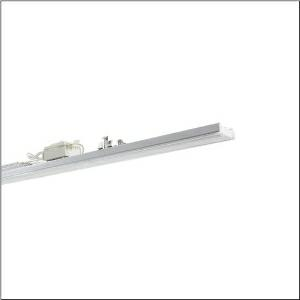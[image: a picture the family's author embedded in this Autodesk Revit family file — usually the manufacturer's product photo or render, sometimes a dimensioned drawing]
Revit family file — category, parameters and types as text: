
# Revit family: licross_r__21_recessed_ho_52te12mn4fxm_584e
name_source: partatom
category: Lighting Fixtures
units: mm (PartAtom-declared; Revit-internal decimal feet)

## family parameters
Cut with Voids When Loaded = No
Host = Face
Light Source = No
Part Type = Normal
Room Calculation Point = No
Round Connector Dimension = Use Diameter
Shared = No

## types (1)
- --- (1 x LED, 15100 lm, 83.1 W, 4000K)
    Apparent Load = 83 VA
    CIE Flux Codes = 69 91 98 100 100
    Color Rendering = 80
    Color Temperature = 4000K
    Default Elevation = 1800 mm
    Description = Licross® 21 Recessed HO, luminaire insert, of sheet steel, galvanised, coil coated, white, length: 1.500mm, width: 66mm, height: 67mm, LED rated luminous flux: 15.100lm, light colour: 840, control gear: ON/OFF Multilumen, with plug, 3-pole, with phase selection, mains connection: 220..240V, AC, 50/60Hz, rated input power: 83W, halogen-free wiring, primary optical cover: cover, of PMMA, light emission: direct distribution, primary light characteristic: symmetric, protection rating (complete): IP54, insulation class (complete): insulation class I (protective earthing), certification: CE, ENEC, VDE, UKCA, protection symbol: D if used in an environment with non-conductive dust loads with corresponding accessories, impact resistance: IK06, permissible ambient temperature for indoor applications: -35..+30°C, corresponds to IFS (International Featured Standards) requirements for safety and quality in the food industry, reducing of maximum allowable ambient temperature of 5°C with ceiling mounting, LABS conformity tested according to VDMA 24364:2018-05, packaging unit: 1 piece
    Height = 58 mm
    Lamp = 1 x LED
    Lamp Light Flux = 15100 lm
    Lamp Power = 83.1 W
    Lamp count = 1
    Length = 1500 mm
    Luminous efficacy = 182 lm/W
    Manufacturer = Siteco
    ModVariant = No
    Model = 52TE12MN4FXM
    Mounting Place = Ceiling
    Mounting Type = Pendant
    Number of Poles = 1
    OnlyDefault = Yes
    Power Factor = 1
    Product Name = Licross® 21 Recessed HO
    Product group = luminaire insert
    ProductGroupID = 902
    Protection Class = Protection class I
    Protection Degree = IP 54
    RLX_Detail_Level = 1
    RLX_Emergency_Light_Flux = 0 lm
    RLX_Emergency_Type = 0
    RLX_Emergency_Type_DB = No
    RlxData = <blob elided: 22305 chars, md5=76ac9ed1>
    Socket = socket
    Standby Power = 0 W
    System Light Flux = 15100 lm
    System Power = 83 W
    Type Comments = factory setting: luminous flux: 100 % | (A | C | E) | 195 mA
    Type Image = l_1296930.jpg
    URL = http://relux.com
    VarID = @adj_103152
    Voltage = 0 V
    Weight = 0.00 kg
    Width = 66 mm

## geometry (parser evidence)
native form markers: Blend x4, Sweep x10
no freeform markers — native parametric forms only
